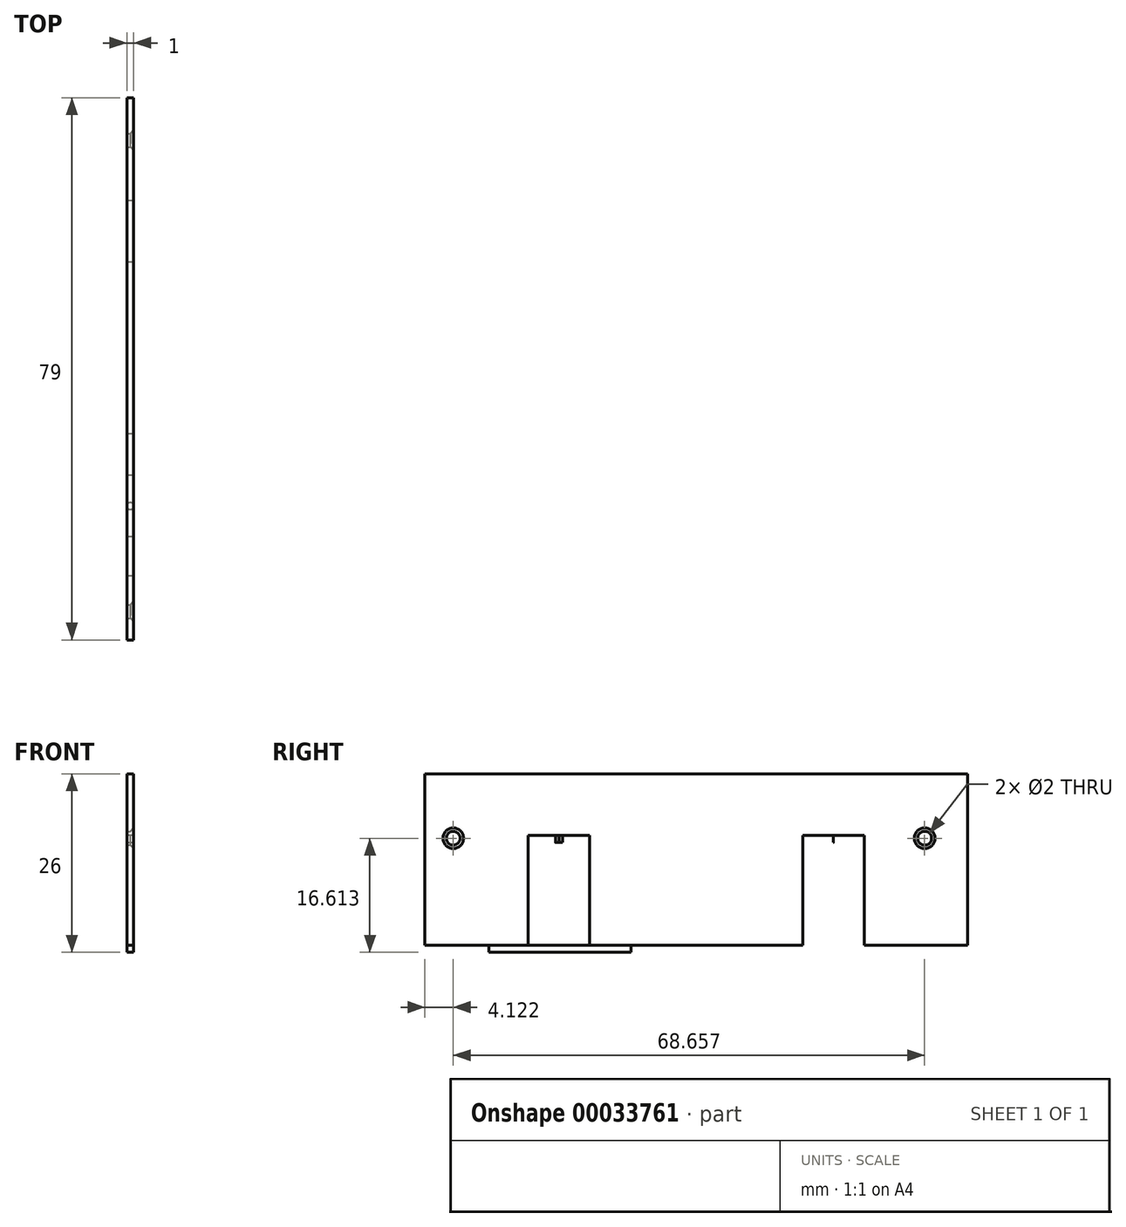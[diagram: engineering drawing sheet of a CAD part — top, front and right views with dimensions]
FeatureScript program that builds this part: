
annotation { "Feature Type Name" : "Feature", "Feature Type Description" : "" }
export const myFeature = defineFeature(function(context is Context, id is Id, definition is map)
    precondition{}
    {
        {
            var Q0;
            Q0=qCreatedBy(makeId("Right.planeOp"),FACE);
            var sketch = newSketch(context, id + "F0", { "sketchPlane" : qUnion([Q0])});
            skLineSegment(sketch, "E0.bottom", {"start": v(-38.32, 25) * mm, "end": v(40.68, 25) * mm});
            skLineSegment(sketch, "E0.top", {"start": v(-38.32, 0) * mm, "end": v(40.68, 0) * mm});
            skLineSegment(sketch, "E0.left", {"start": v(-38.32, 25) * mm, "end": v(-38.32, 0) * mm});
            skLineSegment(sketch, "E0.right", {"start": v(40.68, 25) * mm, "end": v(40.68, 0) * mm});
            skLineSegment(sketch, "E1.top", {"start": v(-23.32, 16) * mm, "end": v(-14.32, 16) * mm});
            skLineSegment(sketch, "E1.left", {"start": v(-23.32, 0) * mm, "end": v(-23.32, 16) * mm});
            skLineSegment(sketch, "E1.right", {"start": v(-14.32, 0) * mm, "end": v(-14.32, 16) * mm});
            skLineSegment(sketch, "E2.top", {"start": v(16.68, 16) * mm, "end": v(25.68, 16) * mm});
            skLineSegment(sketch, "E2.left", {"start": v(16.68, 0) * mm, "end": v(16.68, 16) * mm});
            skLineSegment(sketch, "E2.right", {"start": v(25.68, 0) * mm, "end": v(25.68, 16) * mm});
            skLineSegment(sketch, "E3", {"start": v(-35.07, 16.24) * mm, "end": v(35.62, 16.24) * mm});
            skSolve(sketch);
        }
        {
            var Q0;
            Q0=makeQuery(id+"F0.imprint","IMPRINT",FACE,{"disambiguationData":[TD([[makeQuery(id+"F0.imprint","IMPRINT",EDGE,{"derivedFrom":sQuery(id+"F0.wireOp",EDGE,"E0.bottom")}),-1.0]])]});
            extrude(context, id + "F1", {"entities" : qUnion([Q0]), "depth" : 1 * mm});
        }
        {
            var Q0;
            Q0=makeQuery(id+"F1.opExtrude","CAP_FACE",FACE,{"disambiguationData":[OSD([sQuery(id+"F0.wireOp",EDGE,"E0.bottom"),sQuery(id+"F0.wireOp",EDGE,"E0.top"),sQuery(id+"F0.wireOp",EDGE,"E0.left"),sQuery(id+"F0.wireOp",EDGE,"E0.right"),sQuery(id+"F0.wireOp",EDGE,"E1.top"),sQuery(id+"F0.wireOp",EDGE,"E1.left"),sQuery(id+"F0.wireOp",EDGE,"E1.right"),sQuery(id+"F0.wireOp",EDGE,"E2.top"),sQuery(id+"F0.wireOp",EDGE,"E2.left"),sQuery(id+"F0.wireOp",EDGE,"E2.right")])],"isStart":false});
            var sketch = newSketch(context, id + "F2", { "sketchPlane" : qUnion([Q0])});
            skLineSegment(sketch, "E4", {"start": v(-34.2, 15.61) * mm, "end": v(34.46, 15.61) * mm});
            skSolve(sketch);
        }
        {
            var Q0;
            Q0=sQuery(id+"F2.wireOp",VERTEX,"E4.start");
            var Q1;
            Q1=sQuery(id+"F2.wireOp",VERTEX,"E4.end");
            var Q2;
            Q2=makeQuery(id+"F1.opExtrude","SWEPT_BODY",BODY,{"disambiguationData":[OSD([sQuery(id+"F0.wireOp",EDGE,"E0.bottom"),sQuery(id+"F0.wireOp",EDGE,"E0.top"),sQuery(id+"F0.wireOp",EDGE,"E0.left"),sQuery(id+"F0.wireOp",EDGE,"E0.right"),sQuery(id+"F0.wireOp",EDGE,"E1.top"),sQuery(id+"F0.wireOp",EDGE,"E1.left"),sQuery(id+"F0.wireOp",EDGE,"E1.right"),sQuery(id+"F0.wireOp",EDGE,"E2.top"),sQuery(id+"F0.wireOp",EDGE,"E2.left"),sQuery(id+"F0.wireOp",EDGE,"E2.right")])]});
            hole(context, id + "F3", {"style" : HoleStyle.C_SINK, "holeDiameter" : 2 * mm, "cSinkDiameter" : 3 * mm, "endStyle" : HoleEndStyle.THROUGH, "locations" : qUnion([Q0, Q1]), "scope" : qUnion([Q2]), "cSinkAngle" : 90 * degree});
        }
        {
            var Q0;
            Q0=makeQuery(id+"F1.opExtrude","SWEPT_FACE",FACE,{"disambiguationData":[OSD([sQuery(id+"F0.wireOp",EDGE,"E1.top")])]});
            var sketch = newSketch(context, id + "F4", { "sketchPlane" : qUnion([Q0])});
            skCircle(sketch, "E5", {"center": v(0.5, 18.81) * mm, "radius": 0.5 * mm});
            skPoint(sketch, "E5.first.point", {"position": v(0, 18.82) * mm});
            skPoint(sketch, "E5.second.point", {"position": v(1, 18.82) * mm});
            skPoint(sketch, "E5.third.point", {"position": v(0.5, 19.31) * mm});
            skSolve(sketch);
        }
        {
            var Q0;
            {var subQ0=sQuery(id+"F0.wireOp",EDGE,"E1.top");var subQ2=sQuery(id+"F4.wireOp",EDGE,"E5");var subQ5=makeQuery(id+"F1.opExtrude","CAP_EDGE",EDGE,{"disambiguationData":[OSD([subQ0])],"isStart":true});var subQ7=makeQuery(id+"F4.imprint","INTERSECT",VERTEX,{"disambiguationData":[OD(0.0)],"derivedFrom":[subQ5,subQ2]});Q0=makeQuery(id+"F4.imprint","IMPRINT",FACE,{"disambiguationData":[TD([[makeQuery(id+"F4.imprint","IMPRINT",EDGE,{"disambiguationData":[TD([[subQ7,1.0]])],"derivedFrom":subQ2}),1.0]])]});}
            extrude(context, id + "F5", {"entities" : qUnion([Q0]), "operationType" : NewBodyOperationType.ADD, "depth" : 1 * mm});
        }
        {
            var Q0;
            Q0=makeQuery(id+"F1.opExtrude","SWEPT_FACE",FACE,{"disambiguationData":[OSD([sQuery(id+"F0.wireOp",EDGE,"E2.top")])]});
            var sketch = newSketch(context, id + "F6", { "sketchPlane" : qUnion([Q0])});
            skCircle(sketch, "E6", {"center": v(0.5, -21.15) * mm, "radius": 0.5 * mm});
            skPoint(sketch, "E6.first.point", {"position": v(0, -21.18) * mm});
            skPoint(sketch, "E6.second.point", {"position": v(1, -21.18) * mm});
            skPoint(sketch, "E6.third.point", {"position": v(0.56, -20.66) * mm});
            skSolve(sketch);
        }
        {
            var Q0;
            {var subQ0=sQuery(id+"F0.wireOp",EDGE,"E2.top");var subQ2=sQuery(id+"F6.wireOp",EDGE,"E6");var subQ5=makeQuery(id+"F1.opExtrude","CAP_EDGE",EDGE,{"disambiguationData":[OSD([subQ0])],"isStart":true});var subQ7=makeQuery(id+"F6.imprint","INTERSECT",VERTEX,{"disambiguationData":[OD(0.0)],"derivedFrom":[subQ5,subQ2]});Q0=makeQuery(id+"F6.imprint","IMPRINT",FACE,{"disambiguationData":[TD([[makeQuery(id+"F6.imprint","IMPRINT",EDGE,{"disambiguationData":[TD([[subQ7,1.0]])],"derivedFrom":subQ2}),1.0]])]});}
            extrude(context, id + "F7", {"entities" : qUnion([Q0]), "operationType" : NewBodyOperationType.ADD, "depth" : 1 * mm});
        }
        {
            var Q0;
            {var subQ0=sQuery(id+"F0.wireOp",EDGE,"E0.top");Q0=makeQuery(id+"F1.opExtrude","SWEPT_FACE",FACE,{"disambiguationData":[OSD([subQ0]),TDD([makeQuery(id+"F0.imprint","IMPRINT",EDGE,{"disambiguationData":[TD([[makeQuery(id+"F0.imprint","INTERSECT",VERTEX,{"derivedFrom":[subQ0,sQuery(id+"F0.wireOp",EDGE,"E0.left")]}),-1.0]])],"derivedFrom":subQ0})])]});}
            var sketch = newSketch(context, id + "F8", { "sketchPlane" : qUnion([Q0])});
            skLineSegment(sketch, "E7.bottom", {"start": v(1, 28.99) * mm, "end": v(0, 28.99) * mm});
            skLineSegment(sketch, "E7.top", {"start": v(1, 8.28) * mm, "end": v(0, 8.28) * mm});
            skLineSegment(sketch, "E7.left", {"start": v(1, 28.99) * mm, "end": v(1, 8.28) * mm});
            skLineSegment(sketch, "E7.right", {"start": v(0, 28.99) * mm, "end": v(0, 8.28) * mm});
            skSolve(sketch);
        }
        {
            var Q0;
            Q0 = qSketchRegion(id + "F8", true);
            extrude(context, id + "F9", {"entities" : qUnion([Q0]), "depth" : 1 * mm});
        }
    });
